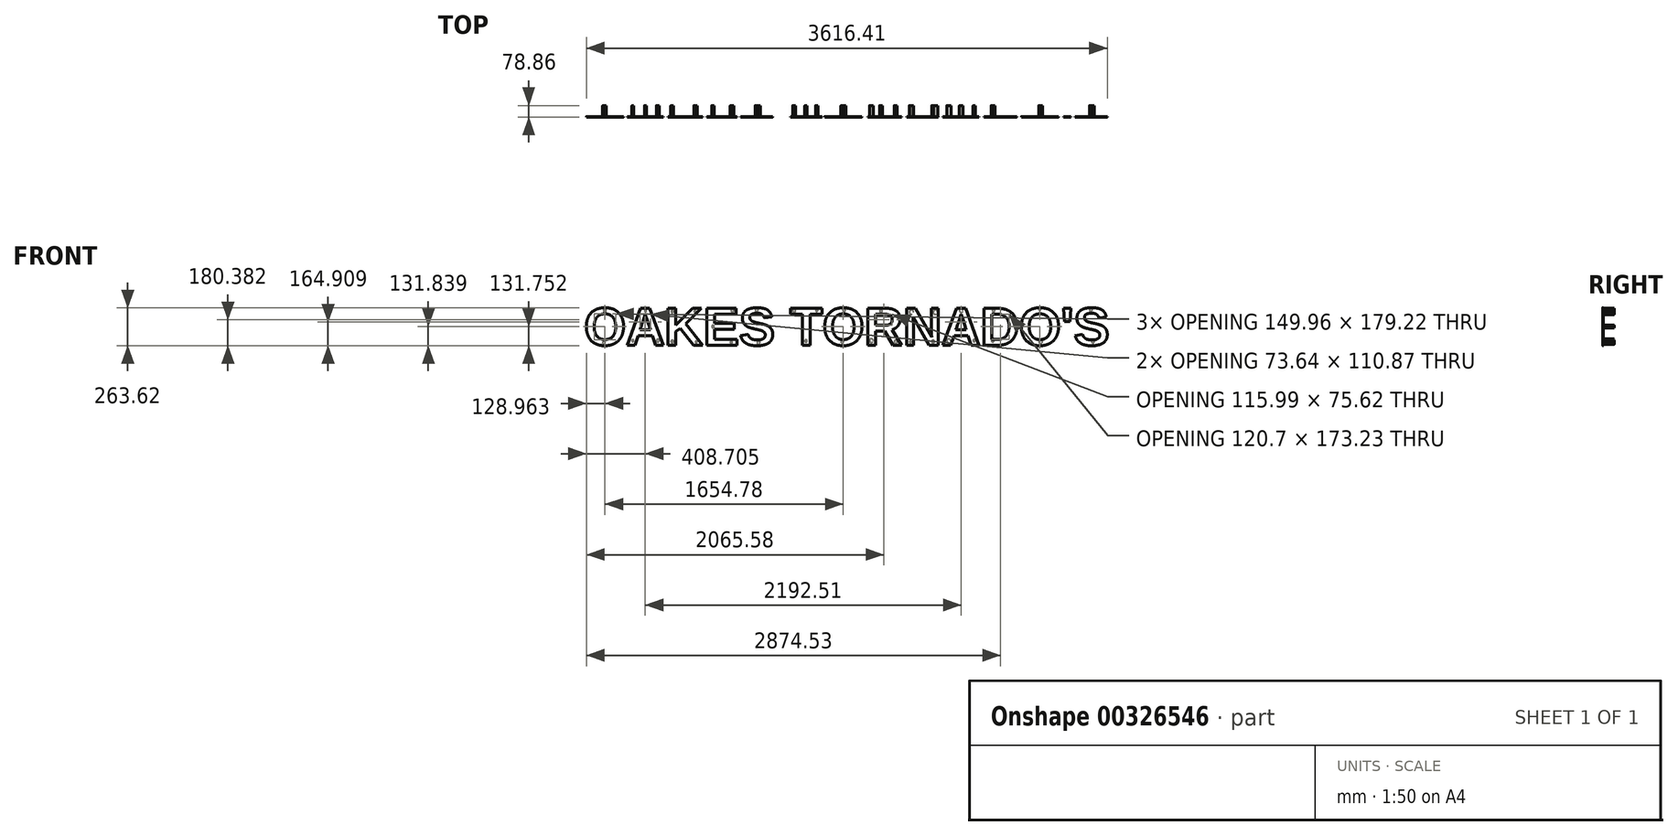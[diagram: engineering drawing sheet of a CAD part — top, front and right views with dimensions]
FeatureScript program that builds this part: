
annotation { "Feature Type Name" : "Feature", "Feature Type Description" : "" }
export const myFeature = defineFeature(function(context is Context, id is Id, definition is map)
    precondition{}
    {
        {
            var Q0;
            Q0=qCreatedBy(makeId("Front.planeOp"),FACE);
            var sketch = newSketch(context, id + "F0", { "sketchPlane" : qUnion([Q0])});
            skText(sketch, "E0", { "text": "OAKES TORNADO\'S", "fontName": "Arimo-Bold.ttf"});
            const initialGuessF0  = {"E0": [-1.8288, 0, 1, 0, 0.26805]};
            skSetInitialGuess(sketch, initialGuessF0);
            skSolve(sketch);
        }
        {
            var Q0;
            Q0 = qSketchRegion(id + "F0", true);
            extrude(context, id + "F1", {"entities" : qUnion([Q0]), "depth" : 2.66 * mm});
        }
        {
            var Q0;
            Q0=makeQuery(id+"F1.opExtrude","CAP_FACE",FACE,{"disambiguationData":[OSD([sQuery(id+"F0.wireOp",EDGE,"E0.sketch_text.stroke-0"),sQuery(id+"F0.wireOp",EDGE,"E0.sketch_text.stroke-1"),sQuery(id+"F0.wireOp",EDGE,"E0.sketch_text.stroke-2"),sQuery(id+"F0.wireOp",EDGE,"E0.sketch_text.stroke-3"),sQuery(id+"F0.wireOp",EDGE,"E0.sketch_text.stroke-4"),sQuery(id+"F0.wireOp",EDGE,"E0.sketch_text.stroke-5"),sQuery(id+"F0.wireOp",EDGE,"E0.sketch_text.stroke-6"),sQuery(id+"F0.wireOp",EDGE,"E0.sketch_text.stroke-7"),sQuery(id+"F0.wireOp",EDGE,"E0.sketch_text.stroke-8"),sQuery(id+"F0.wireOp",EDGE,"E0.sketch_text.stroke-9"),sQuery(id+"F0.wireOp",EDGE,"E0.sketch_text.stroke-10"),sQuery(id+"F0.wireOp",EDGE,"E0.sketch_text.stroke-11"),sQuery(id+"F0.wireOp",EDGE,"E0.sketch_text.stroke-12"),sQuery(id+"F0.wireOp",EDGE,"E0.sketch_text.stroke-13"),sQuery(id+"F0.wireOp",EDGE,"E0.sketch_text.stroke-14"),sQuery(id+"F0.wireOp",EDGE,"E0.sketch_text.stroke-15"),sQuery(id+"F0.wireOp",EDGE,"E0.sketch_text.stroke-16")])],"isStart":true});
            var sketch = newSketch(context, id + "F2", { "sketchPlane" : qUnion([Q0])});
            skCircle(sketch, "E1", {"center": v(-1688.97, 245.87) * mm, "radius": 10.04 * mm});
            skCircle(sketch, "E2", {"center": v(-1703.17, 24.48) * mm, "radius": 9.52 * mm});
            skCircle(sketch, "E3", {"center": v(-1334.18, 248.71) * mm, "radius": 7.24 * mm});
            skCircle(sketch, "E4", {"center": v(-1339.85, 25.9) * mm, "radius": 13.08 * mm});
            skCircle(sketch, "E5", {"center": v(-1013.44, 240.2) * mm, "radius": 8.63 * mm});
            skCircle(sketch, "E6", {"center": v(-1007.77, 33) * mm, "radius": 10.23 * mm});
            skCircle(sketch, "E7", {"center": v(-789.21, 241.62) * mm, "radius": 13.08 * mm});
            skCircle(sketch, "E8", {"center": v(-878.62, 31.58) * mm, "radius": 7.64 * mm});
            skCircle(sketch, "E9", {"center": v(-702.64, 28.74) * mm, "radius": 14.26 * mm});
            skCircle(sketch, "E10", {"center": v(-610.4, 228.84) * mm, "radius": 15.29 * mm});
            skCircle(sketch, "E11", {"center": v(-593.36, 25.9) * mm, "radius": 9.52 * mm});
            skCircle(sketch, "E12", {"center": v(-443.49, 229.49) * mm, "radius": 14.8 * mm});
            skCircle(sketch, "E13", {"center": v(-434.98, 23.23) * mm, "radius": 6.8 * mm});
            skCircle(sketch, "E14", {"center": v(-333.98, 23.23) * mm, "radius": 10.47 * mm});
            skCircle(sketch, "E15", {"center": v(-164.93, 31.58) * mm, "radius": 12.85 * mm});
            skCircle(sketch, "E16", {"center": v(-231.91, 238) * mm, "radius": 9.15 * mm});
            skCircle(sketch, "E17", {"center": v(23.25, 244.37) * mm, "radius": 9.8 * mm});
            skCircle(sketch, "E18", {"center": v(37.07, 22.17) * mm, "radius": 8.57 * mm});
            skCircle(sketch, "E19", {"center": v(214.53, 242.68) * mm, "radius": 8.2 * mm});
            skCircle(sketch, "E20", {"center": v(370.64, 239.5) * mm, "radius": 10.38 * mm});
            skCircle(sketch, "E21", {"center": v(288.6, 29.22) * mm, "radius": 8.2 * mm});
            skCircle(sketch, "E22", {"center": v(630.48, 245) * mm, "radius": 10.46 * mm});
            skCircle(sketch, "E23", {"center": v(618.43, 15.93) * mm, "radius": 11.05 * mm});
            skCircle(sketch, "E24", {"center": v(934.56, 129.26) * mm, "radius": 8.32 * mm});
            skCircle(sketch, "E25", {"center": v(799.26, 240.97) * mm, "radius": 10.46 * mm});
            skCircle(sketch, "E26", {"center": v(1060.47, 235.61) * mm, "radius": 6.83 * mm});
            skCircle(sketch, "E27", {"center": v(1217.2, 234.27) * mm, "radius": 8.99 * mm});
            skCircle(sketch, "E28", {"center": v(1051.1, 21.29) * mm, "radius": 6.83 * mm});
            skCircle(sketch, "E29", {"center": v(1217.2, 25.3) * mm, "radius": 9.47 * mm});
            skCircle(sketch, "E30", {"center": v(1317.66, 31.88) * mm, "radius": 9.55 * mm});
            skCircle(sketch, "E31", {"center": v(1490.46, 32) * mm, "radius": 6.7 * mm});
            skCircle(sketch, "E32", {"center": v(1403.4, 238.3) * mm, "radius": 6.68 * mm});
            skCircle(sketch, "E33", {"center": v(1684.65, 240.81) * mm, "radius": 9.77 * mm});
            skCircle(sketch, "E34", {"center": v(1691.75, 16.4) * mm, "radius": 9.33 * mm});
            skCircle(sketch, "E35", {"center": v(807.06, 20.42) * mm, "radius": 7.64 * mm});
            skSolve(sketch);
        }
        {
            var Q0;
            Q0 = qSketchRegion(id + "F2", true);
            extrude(context, id + "F3", {"entities" : qUnion([Q0]), "depth" : 76.2 * mm});
        }
    });
